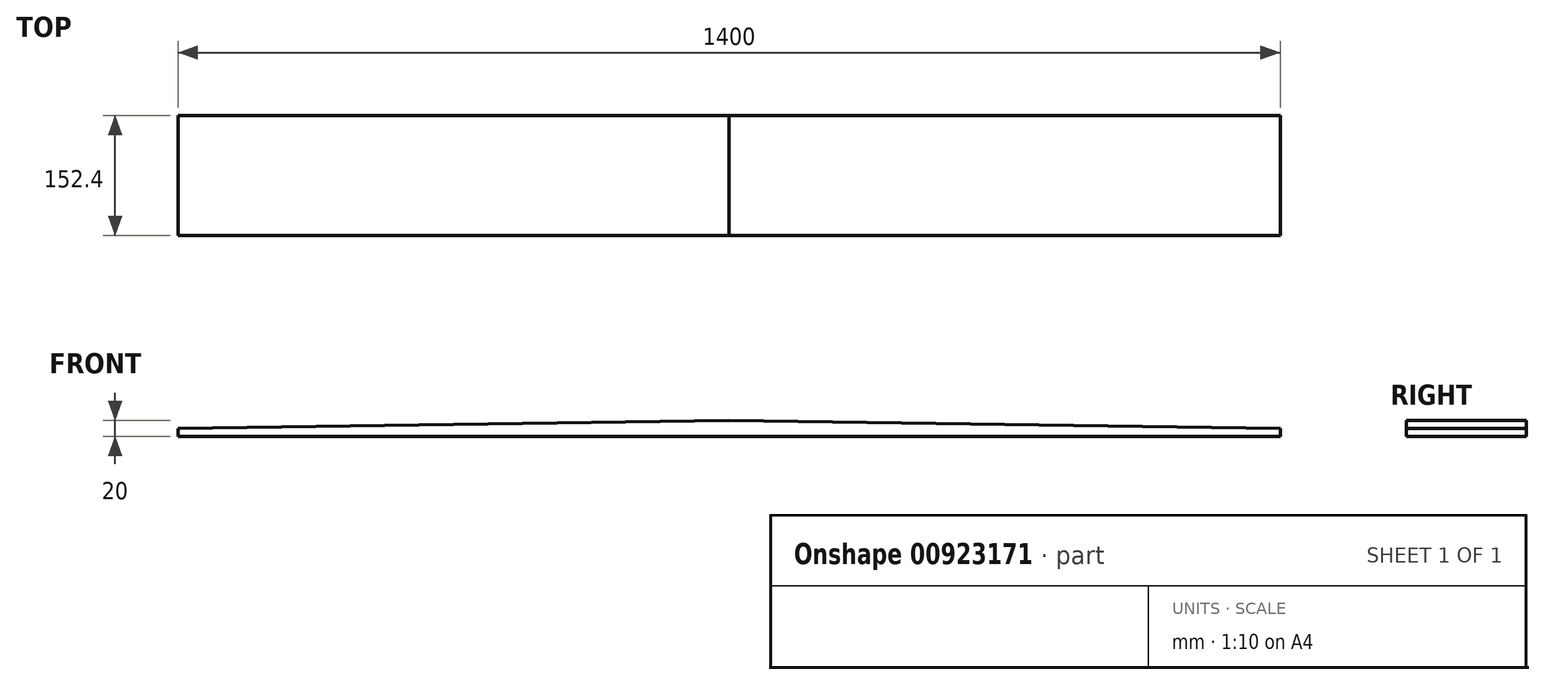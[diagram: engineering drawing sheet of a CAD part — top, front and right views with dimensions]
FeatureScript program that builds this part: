
annotation { "Feature Type Name" : "Feature", "Feature Type Description" : "" }
export const myFeature = defineFeature(function(context is Context, id is Id, definition is map)
    precondition{}
    {
        {
            var Q0;
            Q0=qCreatedBy(makeId("Front.planeOp"),FACE);
            var sketch = newSketch(context, id + "F0", { "sketchPlane" : qUnion([Q0])});
            skLineSegment(sketch, "E0", {"start": v(-700, -10) * mm, "end": v(700, -10) * mm});
            skLineSegment(sketch, "E1", {"start": v(700, -10) * mm, "end": v(700, 0) * mm});
            skLineSegment(sketch, "E2", {"start": v(700, 0) * mm, "end": v(0, 10) * mm});
            skLineSegment(sketch, "E3", {"start": v(0, 10) * mm, "end": v(-700, 0) * mm});
            skLineSegment(sketch, "E4", {"start": v(-700, 0) * mm, "end": v(-700, -10) * mm});
            skSolve(sketch);
        }
        {
            var Q0;
            Q0=makeQuery(id+"F0.imprint","IMPRINT",FACE,{"disambiguationData":[TD([[makeQuery(id+"F0.imprint","IMPRINT",EDGE,{"derivedFrom":sQuery(id+"F0.wireOp",EDGE,"E0")}),1.0]])]});
            extrude(context, id + "F1", {"entities" : qUnion([Q0]), "depth" : 152.4 * mm, "offsetDistance" : 25.4 * mm});
        }
    });
